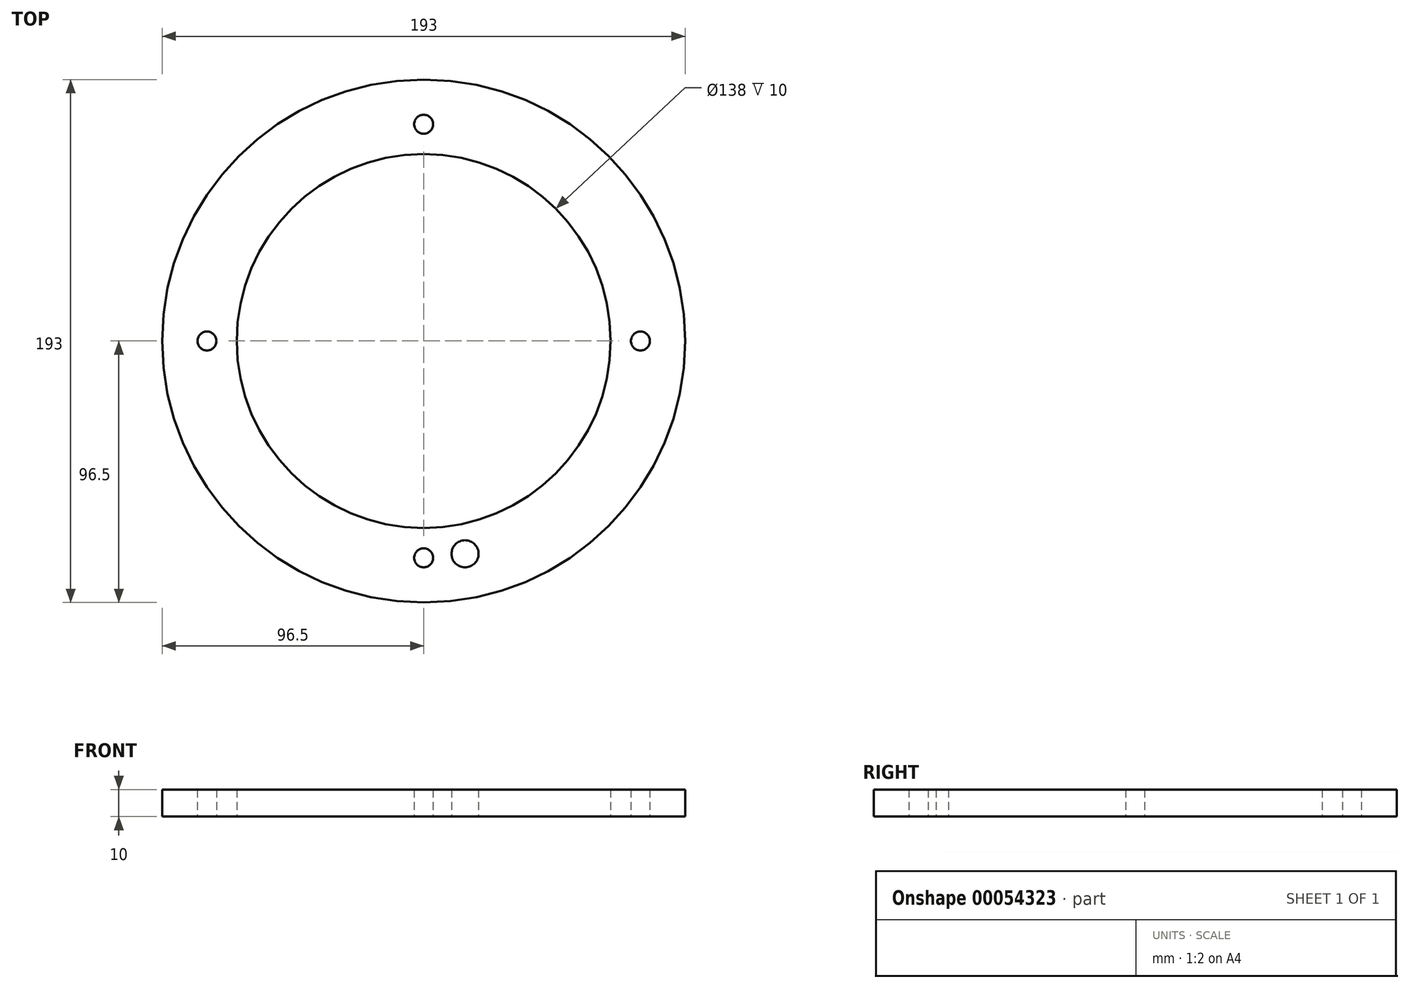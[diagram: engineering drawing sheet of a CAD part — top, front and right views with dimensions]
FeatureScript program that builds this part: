
annotation { "Feature Type Name" : "Feature", "Feature Type Description" : "" }
export const myFeature = defineFeature(function(context is Context, id is Id, definition is map)
    precondition{}
    {
        {
            var Q0;
            Q0=qCreatedBy(makeId("Top.planeOp"),FACE);
            var sketch = newSketch(context, id + "F0", { "sketchPlane" : qUnion([Q0])});
            skCircle(sketch, "E0", {"center": v(0, 0) * mm, "radius": 96.5 * mm});
            skCircle(sketch, "E1", {"center": v(0, 0) * mm, "radius": 69 * mm});
            skCircle(sketch, "E2", {"center": v(15.26, -78.53) * mm, "radius": 5 * mm});
            skCircle(sketch, "E3", {"center": v(0, 0) * mm, "radius": 80 * mm, "construction": true});
            skLineSegment(sketch, "E4", {"start": v(0, 0) * mm, "end": v(24.98, -128.5) * mm, "construction": true});
            skLineSegment(sketch, "E5", {"start": v(0, 0) * mm, "end": v(164.34, 0) * mm, "construction": true});
            skLineSegment(sketch, "E6", {"start": v(164.34, 0) * mm, "end": v(-177.86, 0) * mm, "construction": true});
            skLineSegment(sketch, "E7", {"start": v(0, 0) * mm, "end": v(0, 126.78) * mm, "construction": true});
            skLineSegment(sketch, "E8", {"start": v(0, 126.78) * mm, "end": v(0, -165.87) * mm, "construction": true});
            skCircle(sketch, "E9", {"center": v(-80, 0) * mm, "radius": 3.5 * mm});
            skCircle(sketch, "E10.1.0", {"center": v(0, -80) * mm, "radius": 3.5 * mm});
            skCircle(sketch, "E10.2.0", {"center": v(80, 0) * mm, "radius": 3.5 * mm});
            skCircle(sketch, "E10.3.0", {"center": v(0, 80) * mm, "radius": 3.5 * mm});
            skSolve(sketch);
        }
        {
            var Q0;
            Q0=makeQuery(id+"F0.imprint","IMPRINT",FACE,{"disambiguationData":[TD([[makeQuery(id+"F0.imprint","IMPRINT",EDGE,{"derivedFrom":sQuery(id+"F0.wireOp",EDGE,"E0")}),1.0]])]});
            extrude(context, id + "F1", {"entities" : qUnion([Q0]), "depth" : 10 * mm});
        }
    });
